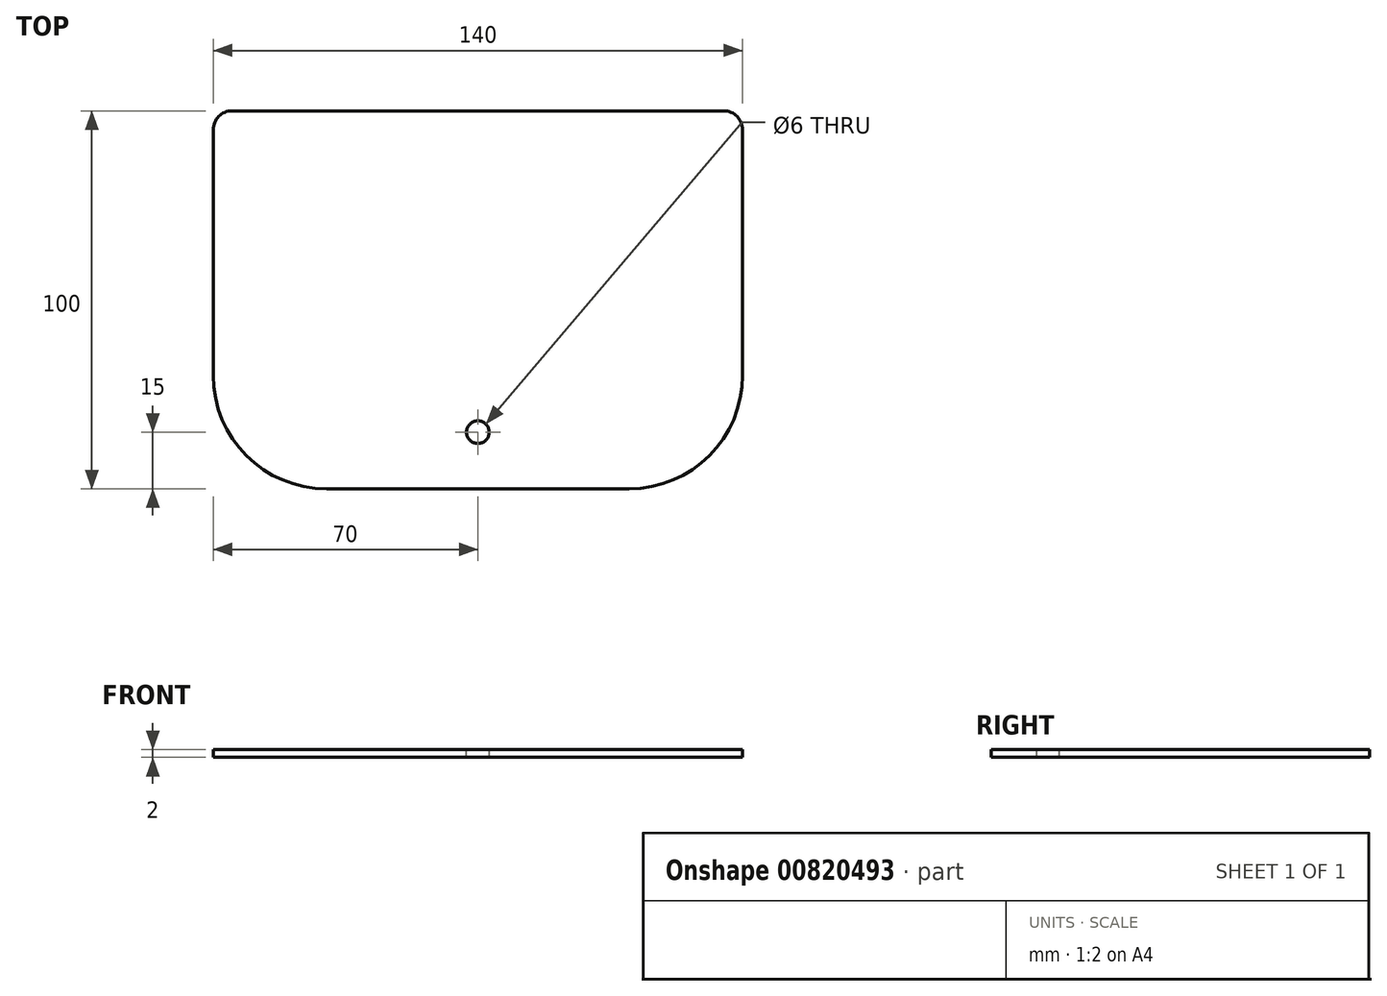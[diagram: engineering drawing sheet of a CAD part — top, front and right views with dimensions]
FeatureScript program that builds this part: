
annotation { "Feature Type Name" : "Feature", "Feature Type Description" : "" }
export const myFeature = defineFeature(function(context is Context, id is Id, definition is map)
    precondition{}
    {
        {
            var Q0;
            Q0=qCreatedBy(makeId("Top.planeOp"),FACE);
            var sketch = newSketch(context, id + "F0", { "sketchPlane" : qUnion([Q0])});
            skLineSegment(sketch, "E0.bottom", {"start": v(70, -50) * mm, "end": v(-70, -50) * mm});
            skLineSegment(sketch, "E0.top", {"start": v(70, 50) * mm, "end": v(-70, 50) * mm});
            skLineSegment(sketch, "E0.left", {"start": v(70, -50) * mm, "end": v(70, 50) * mm});
            skLineSegment(sketch, "E0.right", {"start": v(-70, -50) * mm, "end": v(-70, 50) * mm});
            skPoint(sketch, "E0.middle", {"position": v(0, 0) * mm});
            skSolve(sketch);
        }
        {
            var Q0;
            Q0=makeQuery(id+"F0.imprint","IMPRINT",FACE,{"disambiguationData":[TD([[makeQuery(id+"F0.imprint","IMPRINT",EDGE,{"derivedFrom":sQuery(id+"F0.wireOp",EDGE,"E0.bottom")}),-1.0]])]});
            extrude(context, id + "F1", {"entities" : qUnion([Q0]), "depth" : 2 * mm, "offsetDistance" : 25 * mm});
        }
        {
            var Q0;
            {var subQ0=sQuery(id+"F0.wireOp",EDGE,"E0.right");var subQ1=sQuery(id+"F0.wireOp",EDGE,"E0.bottom");Q0=makeQuery(id+"F9IUGif73eA3r8j_1.boolean.opBoolean","MERGE",EDGE,{"derivedFrom":[makeQuery(id+"F1.opExtrude","SWEPT_EDGE",EDGE,{"disambiguationData":[OSD([subQ1,subQ0])]}),makeQuery(id+"F9IUGif73eA3r8j_1.opExtrude","SWEPT_EDGE",EDGE,{"disambiguationData":[OSD([subQ1,subQ0])]})]});}
            var Q1;
            Q1=makeQuery(id+"F9IUGif73eA3r8j_1.opExtrude","SWEPT_EDGE",EDGE,{"disambiguationData":[OSD([sQuery(id+"FQjfjUhFkGEVaxD_1.wireOp",EDGE,"98dd9e88-5a0e-4900-a529-5099e3b0fa91.0"),sQuery(id+"FQjfjUhFkGEVaxD_1.wireOp",EDGE,"98dd9e88-5a0e-4900-a529-5099e3b0fa91.1")])]});
            var Q2;
            {var subQ0=sQuery(id+"F0.wireOp",EDGE,"E0.left");var subQ1=sQuery(id+"F0.wireOp",EDGE,"E0.bottom");Q2=makeQuery(id+"F9IUGif73eA3r8j_1.boolean.opBoolean","MERGE",EDGE,{"derivedFrom":[makeQuery(id+"F1.opExtrude","SWEPT_EDGE",EDGE,{"disambiguationData":[OSD([subQ1,subQ0])]}),makeQuery(id+"F9IUGif73eA3r8j_1.opExtrude","SWEPT_EDGE",EDGE,{"disambiguationData":[OSD([subQ1,subQ0])]})]});}
            var Q3;
            Q3=makeQuery(id+"F9IUGif73eA3r8j_1.opExtrude","SWEPT_EDGE",EDGE,{"disambiguationData":[OSD([sQuery(id+"FQjfjUhFkGEVaxD_1.wireOp",EDGE,"98dd9e88-5a0e-4900-a529-5099e3b0fa91.1"),sQuery(id+"FQjfjUhFkGEVaxD_1.wireOp",EDGE,"98dd9e88-5a0e-4900-a529-5099e3b0fa91.2")])]});
            fillet(context, id + "F2", {"entities" : qUnion([Q0, Q1, Q2, Q3]), "radius" : 30 * mm, "tangentPropagation" : true, "allowEdgeOverflow" : false});
        }
        {
            var Q0;
            Q0=makeQuery(id+"F1.opExtrude","CAP_FACE",FACE,{"disambiguationData":[OSD([sQuery(id+"F0.wireOp",EDGE,"E0.bottom"),sQuery(id+"F0.wireOp",EDGE,"E0.top"),sQuery(id+"F0.wireOp",EDGE,"E0.left"),sQuery(id+"F0.wireOp",EDGE,"E0.right")])],"isStart":false});
            var sketch = newSketch(context, id + "F3", { "sketchPlane" : qUnion([Q0])});
            skCircle(sketch, "E1", {"center": v(0, -35) * mm, "radius": 3 * mm});
            skPoint(sketch, "E1.centerSnap0", {"position": v(0, -45) * mm});
            skSolve(sketch);
        }
        {
            var Q0;
            Q0=makeQuery(id+"F3.imprint","IMPRINT",FACE,{"disambiguationData":[TD([[makeQuery(id+"F3.imprint","IMPRINT",EDGE,{"derivedFrom":sQuery(id+"F3.wireOp",EDGE,"E1")}),1.0]])]});
            extrude(context, id + "F4", {"entities" : qUnion([Q0]), "operationType" : NewBodyOperationType.REMOVE, "oppositeDirection" : true, "depth" : 25 * mm, "offsetDistance" : 25 * mm});
        }
        {
            var Q0;
            Q0=makeQuery(id+"F1.opExtrude","SWEPT_EDGE",EDGE,{"disambiguationData":[OSD([sQuery(id+"F0.wireOp",EDGE,"E0.top"),sQuery(id+"F0.wireOp",EDGE,"E0.left")])]});
            var Q1;
            Q1=makeQuery(id+"F1.opExtrude","SWEPT_EDGE",EDGE,{"disambiguationData":[OSD([sQuery(id+"F0.wireOp",EDGE,"E0.top"),sQuery(id+"F0.wireOp",EDGE,"E0.right")])]});
            fillet(context, id + "F5", {"entities" : qUnion([Q0, Q1]), "radius" : 5 * mm, "tangentPropagation" : true, "allowEdgeOverflow" : false});
        }
    });
